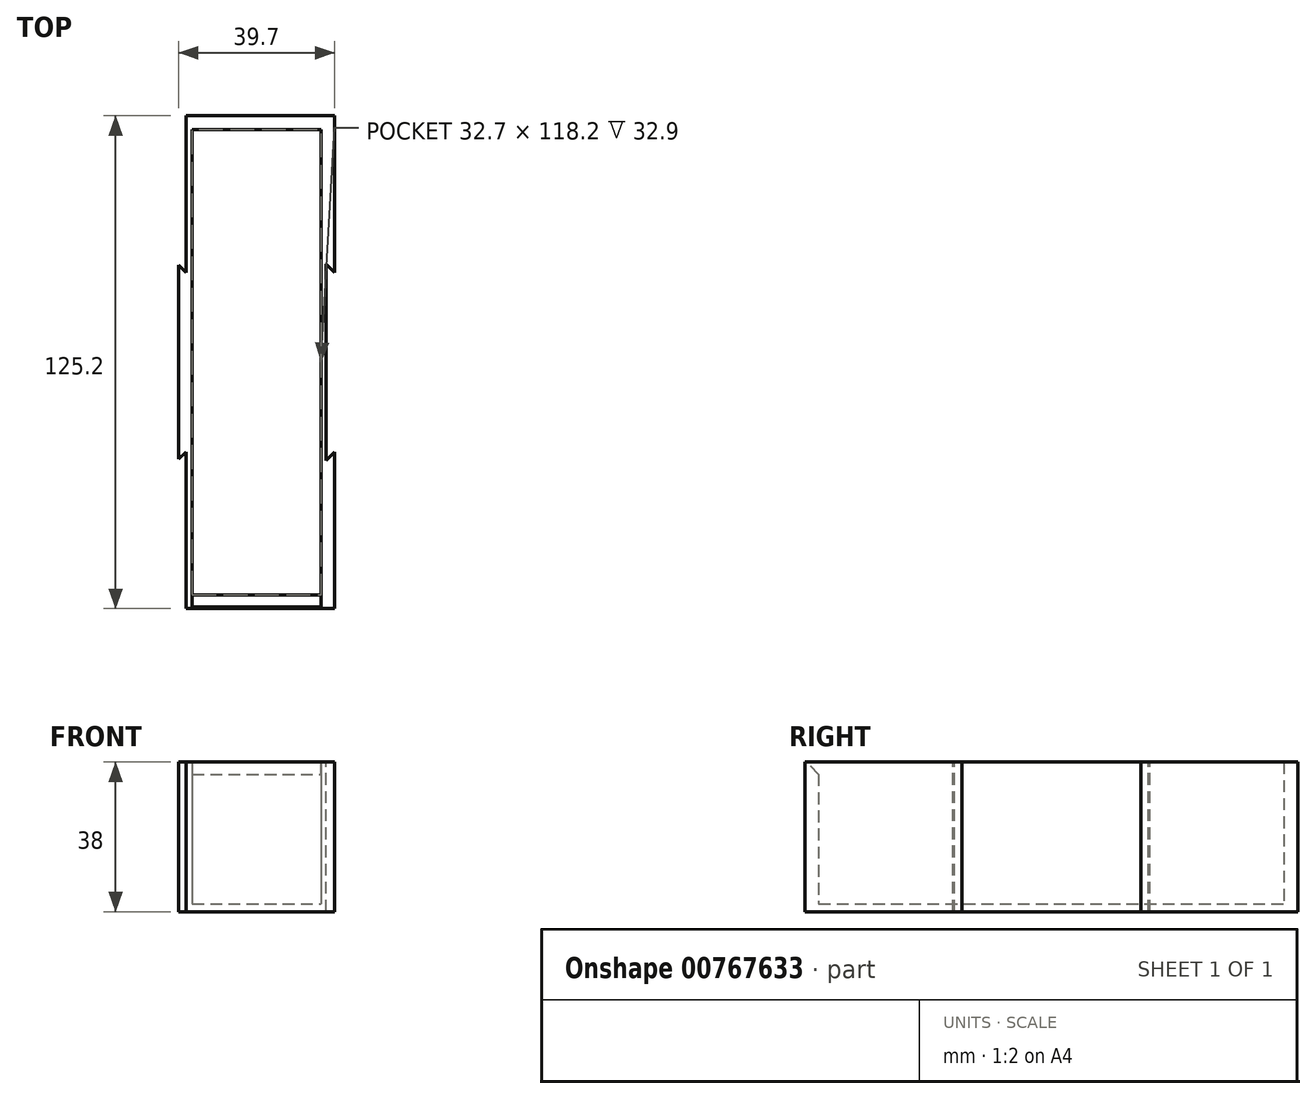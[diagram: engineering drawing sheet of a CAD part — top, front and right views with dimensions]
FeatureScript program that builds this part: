
annotation { "Feature Type Name" : "Feature", "Feature Type Description" : "" }
export const myFeature = defineFeature(function(context is Context, id is Id, definition is map)
    precondition{}
    {
        {
            var Q0;
            Q0=qCreatedBy(makeId("Top.planeOp"),FACE);
            var sketch = newSketch(context, id + "F0", { "sketchPlane" : qUnion([Q0])});
            skLineSegment(sketch, "E0.bottom", {"start": v(16.35, 59.1) * mm, "end": v(-16.35, 59.1) * mm});
            skLineSegment(sketch, "E0.top", {"start": v(16.35, -59.1) * mm, "end": v(-16.35, -59.1) * mm});
            skLineSegment(sketch, "E0.left", {"start": v(16.35, 59.1) * mm, "end": v(16.35, -59.1) * mm});
            skLineSegment(sketch, "E0.right", {"start": v(-16.35, 59.1) * mm, "end": v(-16.35, -59.1) * mm});
            skPoint(sketch, "E0.middle", {"position": v(0, 0) * mm});
            skLineSegment(sketch, "E1.bottom", {"start": v(19.85, -62.6) * mm, "end": v(-19.85, -62.6) * mm});
            skLineSegment(sketch, "E1.top", {"start": v(19.85, 62.6) * mm, "end": v(-19.85, 62.6) * mm});
            skLineSegment(sketch, "E1.left", {"start": v(19.85, -62.6) * mm, "end": v(19.85, 62.6) * mm});
            skLineSegment(sketch, "E1.right", {"start": v(-19.85, -62.6) * mm, "end": v(-19.85, 62.6) * mm});
            skSolve(sketch);
        }
        {
            var Q0;
            Q0=qSketchRegion(id+"F0",true);
            var Q1;
            Q1=makeQuery(id+"F0.imprint","IMPRINT",FACE,{"disambiguationData":[TD([[makeQuery(id+"F0.imprint","IMPRINT",EDGE,{"derivedFrom":sQuery(id+"F0.wireOp",EDGE,"E0.bottom")}),1.0]])]});
            extrude(context, id + "F1", {"entities" : qUnion([Q0, Q1]), "depth" : 2 * mm, "offsetDistance" : 25 * mm});
        }
        {
            var Q0;
            Q0=makeQuery(id+"F0.imprint","IMPRINT",FACE,{"disambiguationData":[TD([[makeQuery(id+"F0.imprint","IMPRINT",EDGE,{"derivedFrom":sQuery(id+"F0.wireOp",EDGE,"E0.bottom")}),-1.0]])]});
            extrude(context, id + "F2", {"entities" : qUnion([Q0]), "operationType" : NewBodyOperationType.ADD, "depth" : 38 * mm, "offsetDistance" : 25 * mm});
        }
        {
            var Q0;
            Q0=makeQuery(id+"F2.opExtrude","CAP_FACE",FACE,{"disambiguationData":[OSD([sQuery(id+"F0.wireOp",EDGE,"E0.bottom"),sQuery(id+"F0.wireOp",EDGE,"E0.top"),sQuery(id+"F0.wireOp",EDGE,"E0.left"),sQuery(id+"F0.wireOp",EDGE,"E0.right"),sQuery(id+"F0.wireOp",EDGE,"E1.bottom"),sQuery(id+"F0.wireOp",EDGE,"E1.top"),sQuery(id+"F0.wireOp",EDGE,"E1.left"),sQuery(id+"F0.wireOp",EDGE,"E1.right")])],"isStart":false});
            var sketch = newSketch(context, id + "F3", { "sketchPlane" : qUnion([Q0])});
            skLineSegment(sketch, "E2", {"start": v(19.85, 22.75) * mm, "end": v(17.6, 25) * mm});
            skLineSegment(sketch, "E3", {"start": v(17.6, 25) * mm, "end": v(17.6, -25) * mm});
            skLineSegment(sketch, "E4", {"start": v(-19.85, 24.65) * mm, "end": v(-17.95, 22.75) * mm});
            skLineSegment(sketch, "E5", {"start": v(-19.85, -24.65) * mm, "end": v(-17.95, -22.75) * mm});
            skLineSegment(sketch, "E6", {"start": v(-17.95, -22.75) * mm, "end": v(-17.95, 22.75) * mm, "construction": true});
            skLineSegment(sketch, "E7", {"start": v(-17.95, 22.75) * mm, "end": v(-17.95, 62.6) * mm});
            skLineSegment(sketch, "E8", {"start": v(-17.95, 62.6) * mm, "end": v(-19.85, 62.6) * mm});
            skLineSegment(sketch, "E9", {"start": v(-19.85, 62.6) * mm, "end": v(-19.85, 24.65) * mm});
            skLineSegment(sketch, "E10", {"start": v(-17.95, -22.75) * mm, "end": v(-17.95, -62.6) * mm});
            skLineSegment(sketch, "E11", {"start": v(-17.95, -62.6) * mm, "end": v(-19.85, -62.6) * mm});
            skLineSegment(sketch, "E12", {"start": v(-19.85, -62.6) * mm, "end": v(-19.85, -24.65) * mm});
            skLineSegment(sketch, "E13", {"start": v(-19.85, 25) * mm, "end": v(-17.95, 23.1) * mm, "construction": true});
            skLineSegment(sketch, "E14", {"start": v(-19.85, -25) * mm, "end": v(-17.95, -23.1) * mm, "construction": true});
            skLineSegment(sketch, "E15", {"start": v(19.85, 22.75) * mm, "end": v(19.85, -22.75) * mm});
            skLineSegment(sketch, "E16", {"start": v(19.85, -22.75) * mm, "end": v(17.6, -25) * mm});
            skPoint(sketch, "E17", {"position": v(17.6, 0) * mm});
            skSolve(sketch);
        }
        {
            var Q0;
            {var subQ0=sQuery(id+"F3.wireOp",EDGE,"E8");Q0=makeQuery(id+"F3.imprint","IMPRINT",FACE,{"disambiguationData":[TD([[makeQuery(id+"F3.imprint","IMPRINT",EDGE,{"derivedFrom":subQ0}),1.0]])]});}
            var Q1;
            {var subQ0=sQuery(id+"F3.wireOp",EDGE,"E11");Q1=makeQuery(id+"F3.imprint","IMPRINT",FACE,{"disambiguationData":[TD([[makeQuery(id+"F3.imprint","IMPRINT",EDGE,{"derivedFrom":subQ0}),-1.0]])]});}
            var Q2;
            {var subQ0=sQuery(id+"F3.wireOp",EDGE,"E14");Q2=makeQuery(id+"F3.imprint","IMPRINT",FACE,{"disambiguationData":[TD([[makeQuery(id+"F3.imprint","IMPRINT",EDGE,{"derivedFrom":subQ0}),-1.0]])]});}
            var Q3;
            Q3=makeQuery(id+"F3.imprint","IMPRINT",FACE,{"disambiguationData":[TD([[makeQuery(id+"F3.imprint","IMPRINT",EDGE,{"derivedFrom":sQuery(id+"F3.wireOp",EDGE,"E2")}),1.0]])]});
            extrude(context, id + "F4", {"entities" : qUnion([Q0, Q1, Q2, Q3]), "operationType" : NewBodyOperationType.REMOVE, "endBound" : BoundingType.THROUGH_ALL, "oppositeDirection" : true, "depth" : 25 * mm, "offsetDistance" : 25 * mm});
        }
        {
            var Q0;
            Q0=makeQuery(id+"F2.opExtrude","CAP_EDGE",EDGE,{"disambiguationData":[OSD([sQuery(id+"F0.wireOp",EDGE,"E0.top")])],"isStart":false});
            chamfer(context, id + "F5", {"entities" : qUnion([Q0]), "width" : 3.1 * mm, "tangentPropagation" : true});
        }
    });
